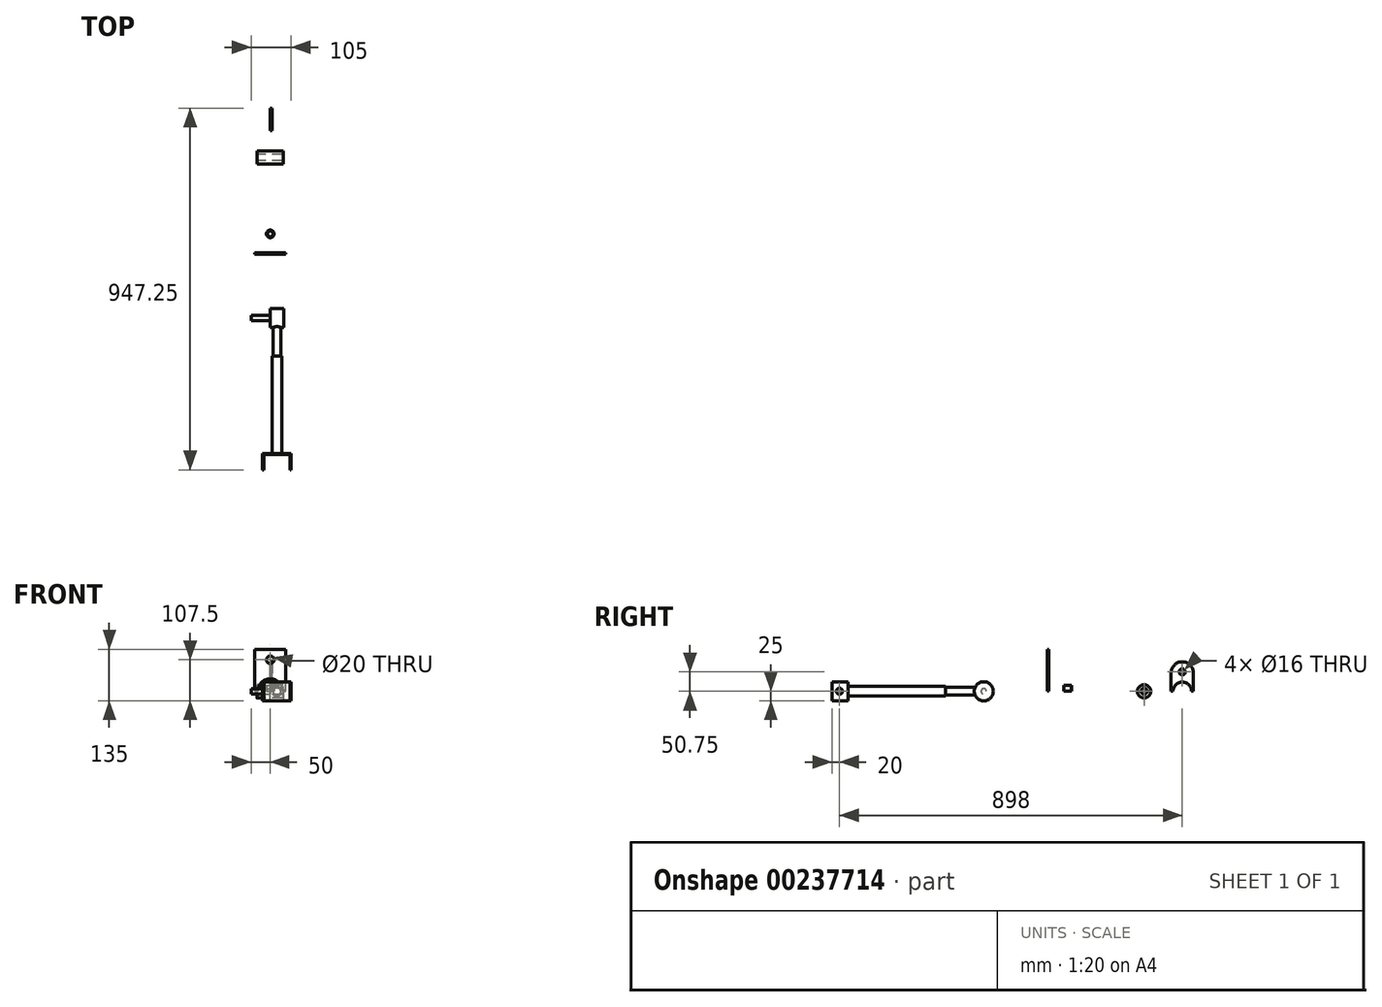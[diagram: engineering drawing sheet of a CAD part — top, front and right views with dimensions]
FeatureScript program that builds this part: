
annotation { "Feature Type Name" : "Feature", "Feature Type Description" : "" }
export const myFeature = defineFeature(function(context is Context, id is Id, definition is map)
    precondition{}
    {
        {
            var Q0;
            Q0=qCreatedBy(makeId("Front.planeOp"),FACE);
            var sketch = newSketch(context, id + "F0", { "sketchPlane" : qUnion([Q0])});
            skArc(sketch, "E0", {"start": v(32.5, 0) * mm, "mid": v(0, 32.5) * mm, "end": v(-32.5, 0) * mm});
            skLineSegment(sketch, "E1.bottom", {"start": v(-40.5, 0) * mm, "end": v(-32.5, 0) * mm});
            skLineSegment(sketch, "E1.top", {"start": v(-40.5, 110) * mm, "end": v(40.5, 110) * mm});
            skLineSegment(sketch, "E1.left", {"start": v(-40.5, 0) * mm, "end": v(-40.5, 110) * mm});
            skLineSegment(sketch, "E1.right", {"start": v(40.5, 0) * mm, "end": v(40.5, 110) * mm});
            skLineSegment(sketch, "E2.trimOffspring", {"start": v(32.5, 0) * mm, "end": v(40.5, 0) * mm});
            skCircle(sketch, "E3", {"center": v(0, 82.5) * mm, "radius": 10 * mm});
            skSolve(sketch);
        }
        {
            var Q0;
            Q0=makeQuery(id+"F0.imprint","IMPRINT",FACE,{"disambiguationData":[TD([[makeQuery(id+"F0.imprint","IMPRINT",EDGE,{"derivedFrom":sQuery(id+"F0.wireOp",EDGE,"E0")}),-1.0]])]});
            extrude(context, id + "F1", {"entities" : qUnion([Q0]), "depth" : 3 * mm});
        }
        {
            var Q0;
            Q0=qCreatedBy(makeId("Right.planeOp"),FACE);
            var sketch = newSketch(context, id + "F2", { "sketchPlane" : qUnion([Q0])});
            skCircle(sketch, "E4", {"center": v(-170, 0) * mm, "radius": 25 * mm});
            skSolve(sketch);
        }
        {
            var Q0;
            Q0 = qSketchRegion(id + "F2", true);
            extrude(context, id + "F3", {"entities" : qUnion([Q0]), "depth" : 35 * mm});
        }
        {
            var Q0;
            Q0=makeQuery(id+"F3.opExtrude","CAP_FACE",FACE,{"disambiguationData":[OSD([sQuery(id+"F2.wireOp",EDGE,"E4")])],"isStart":true});
            var sketch = newSketch(context, id + "F4", { "sketchPlane" : qUnion([Q0])});
            skCircle(sketch, "E5", {"center": v(170, 0) * mm, "radius": 7 * mm});
            skSolve(sketch);
        }
        {
            var Q0;
            Q0=makeQuery(id+"F4.imprint","IMPRINT",FACE,{"disambiguationData":[TD([[makeQuery(id+"F4.imprint","IMPRINT",EDGE,{"derivedFrom":sQuery(id+"F4.wireOp",EDGE,"E5")}),1.0]])]});
            extrude(context, id + "F5", {"entities" : qUnion([Q0]), "operationType" : NewBodyOperationType.ADD, "depth" : 50 * mm});
        }
        {
            var Q0;
            Q0=qCreatedBy(makeId("Front.planeOp"),FACE);
            cPlane(context, id + "F6", {"entities" : qUnion([Q0]), "cplaneType" : CPlaneType.OFFSET, "offset" : 170 * mm, "width" : 150 * mm, "height" : 150 * mm});
        }
        {
            var Q0;
            Q0=qCreatedBy(id+"F6.planeOp",FACE);
            var sketch = newSketch(context, id + "F7", { "sketchPlane" : qUnion([Q0])});
            skCircle(sketch, "E6", {"center": v(17.5, 0) * mm, "radius": 10 * mm});
            skSolve(sketch);
        }
        {
            var Q0;
            Q0 = qSketchRegion(id + "F7", true);
            extrude(context, id + "F8", {"entities" : qUnion([Q0]), "operationType" : NewBodyOperationType.ADD, "depth" : 100 * mm});
        }
        {
            var Q0;
            Q0=makeQuery(id+"F8.opExtrude","CAP_FACE",FACE,{"disambiguationData":[OSD([sQuery(id+"F7.wireOp",EDGE,"E6")])],"isStart":false});
            var sketch = newSketch(context, id + "F9", { "sketchPlane" : qUnion([Q0])});
            skCircle(sketch, "E7", {"center": v(17.5, 0) * mm, "radius": 12.7 * mm});
            skSolve(sketch);
        }
        {
            var Q0;
            Q0 = qSketchRegion(id + "F9", true);
            var Q1;
            Q1=sQuery(id+"F9.wireOp",EDGE,"E7");
            extrude(context, id + "F10", {"entities" : qUnion([Q0]), "operationType" : NewBodyOperationType.ADD, "surfaceEntities" : qUnion([Q1]), "depth" : 255 * mm});
        }
        {
            var Q0;
            Q0=qCreatedBy(makeId("Top.planeOp"),FACE);
            var sketch = newSketch(context, id + "F11", { "sketchPlane" : qUnion([Q0])});
            skLineSegment(sketch, "E8.top", {"start": v(-17, -528) * mm, "end": v(52, -528) * mm});
            skLineSegment(sketch, "E8.left", {"start": v(-17, -568) * mm, "end": v(-17, -528) * mm});
            skLineSegment(sketch, "E8.right", {"start": v(52, -568) * mm, "end": v(52, -528) * mm});
            skLineSegment(sketch, "E9", {"start": v(-17, -568) * mm, "end": v(-20, -568) * mm});
            skLineSegment(sketch, "E10", {"start": v(-20, -568) * mm, "end": v(-20, -525) * mm});
            skLineSegment(sketch, "E11", {"start": v(-20, -525) * mm, "end": v(55, -525) * mm});
            skLineSegment(sketch, "E12", {"start": v(55, -525) * mm, "end": v(55, -568) * mm});
            skLineSegment(sketch, "E13", {"start": v(55, -568) * mm, "end": v(52, -568) * mm});
            skSolve(sketch);
        }
        {
            var Q0;
            Q0=makeQuery(id+"F11.imprint","IMPRINT",FACE,{"disambiguationData":[TD([[makeQuery(id+"F11.imprint","IMPRINT",EDGE,{"derivedFrom":sQuery(id+"F11.wireOp",EDGE,"E8.top")}),1.0]])]});
            extrude(context, id + "F12", {"entities" : qUnion([Q0]), "operationType" : NewBodyOperationType.ADD, "endBound" : BoundingType.SYMMETRIC, "depth" : 50 * mm});
        }
        {
            var Q0;
            Q0=makeQuery(id+"F12.opExtrude","SWEPT_FACE",FACE,{"disambiguationData":[OSD([sQuery(id+"F11.wireOp",EDGE,"E12")])]});
            var sketch = newSketch(context, id + "F13", { "sketchPlane" : qUnion([Q0])});
            skCircle(sketch, "E14", {"center": v(-548, 0) * mm, "radius": 8 * mm});
            skSolve(sketch);
        }
        {
            var Q0;
            Q0=makeQuery(id+"F13.imprint","IMPRINT",FACE,{"disambiguationData":[TD([[makeQuery(id+"F13.imprint","IMPRINT",EDGE,{"derivedFrom":sQuery(id+"F13.wireOp",EDGE,"E14")}),1.0]])]});
            extrude(context, id + "F14", {"entities" : qUnion([Q0]), "operationType" : NewBodyOperationType.REMOVE, "oppositeDirection" : true, "depth" : 82.4 * mm});
        }
        {
            var Q0;
            Q0=qCreatedBy(makeId("Right.planeOp"),FACE);
            var sketch = newSketch(context, id + "F15", { "sketchPlane" : qUnion([Q0])});
            skCircle(sketch, "E15", {"center": v(250, 0) * mm, "radius": 17.5 * mm});
            skCircle(sketch, "E16", {"center": v(250, 0) * mm, "radius": 8 * mm});
            skSolve(sketch);
        }
        {
            var Q0;
            Q0=makeQuery(id+"F15.imprint","IMPRINT",FACE,{"disambiguationData":[TD([[makeQuery(id+"F15.imprint","IMPRINT",EDGE,{"derivedFrom":sQuery(id+"F15.wireOp",EDGE,"E15")}),1.0]])]});
            extrude(context, id + "F16", {"entities" : qUnion([Q0]), "endBound" : BoundingType.SYMMETRIC, "depth" : 69 * mm});
        }
        {
            var Q0;
            Q0=qCreatedBy(makeId("Right.planeOp"),FACE);
            var sketch = newSketch(context, id + "F17", { "sketchPlane" : qUnion([Q0])});
            skArc(sketch, "E17", {"start": v(374.25, 0) * mm, "mid": v(350, 24.25) * mm, "end": v(325.75, 0) * mm});
            skLineSegment(sketch, "E18.bottom", {"start": v(379.25, 0) * mm, "end": v(374.25, 0) * mm});
            skLineSegment(sketch, "E18.left", {"start": v(379.25, 0) * mm, "end": v(379.25, 48) * mm});
            skLineSegment(sketch, "E18.right", {"start": v(320.75, 0) * mm, "end": v(320.75, 48) * mm});
            skLineSegment(sketch, "E19.trimOffspring", {"start": v(325.75, 0) * mm, "end": v(320.75, 0) * mm});
            skArc(sketch, "E20", {"start": v(379.25, 48) * mm, "mid": v(350, 77.25) * mm, "end": v(320.75, 48) * mm});
            skCircle(sketch, "E21", {"center": v(350, 50.75) * mm, "radius": 8 * mm});
            skSolve(sketch);
        }
        {
            var Q0;
            Q0=makeQuery(id+"F17.imprint","IMPRINT",FACE,{"disambiguationData":[TD([[makeQuery(id+"F17.imprint","IMPRINT",EDGE,{"derivedFrom":sQuery(id+"F17.wireOp",EDGE,"E17")}),-1.0]])]});
            extrude(context, id + "F18", {"entities" : qUnion([Q0]), "depth" : 5 * mm});
        }
        {
            var Q0;
            Q0=qCreatedBy(makeId("Right.planeOp"),FACE);
            var sketch = newSketch(context, id + "F19", { "sketchPlane" : qUnion([Q0])});
            skLineSegment(sketch, "E22", {"start": v(58, 15) * mm, "end": v(60, 15) * mm});
            skLineSegment(sketch, "E23", {"start": v(60, 15) * mm, "end": v(60, 0) * mm});
            skLineSegment(sketch, "E24", {"start": v(50, 0) * mm, "end": v(50, 86.75) * mm});
            skLineSegment(sketch, "E25", {"start": v(60, 0) * mm, "end": v(57.25, 0) * mm});
            skLineSegment(sketch, "E26", {"start": v(57.25, 0) * mm, "end": v(58, 15) * mm});
            skSolve(sketch);
        }
        {
            var Q0;
            Q0=makeQuery(id+"F19.imprint","IMPRINT",FACE,{"disambiguationData":[TD([[makeQuery(id+"F19.imprint","IMPRINT",EDGE,{"derivedFrom":sQuery(id+"F19.wireOp",EDGE,"E22")}),-1.0]])]});
            var Q1;
            Q1=sQuery(id+"F19.wireOp",EDGE,"E24");
            revolve(context, id + "F20", {"entities" : qUnion([Q0]), "axis" : qUnion([Q1]), "revolveType" : RevolveType.FULL});
        }
    });
